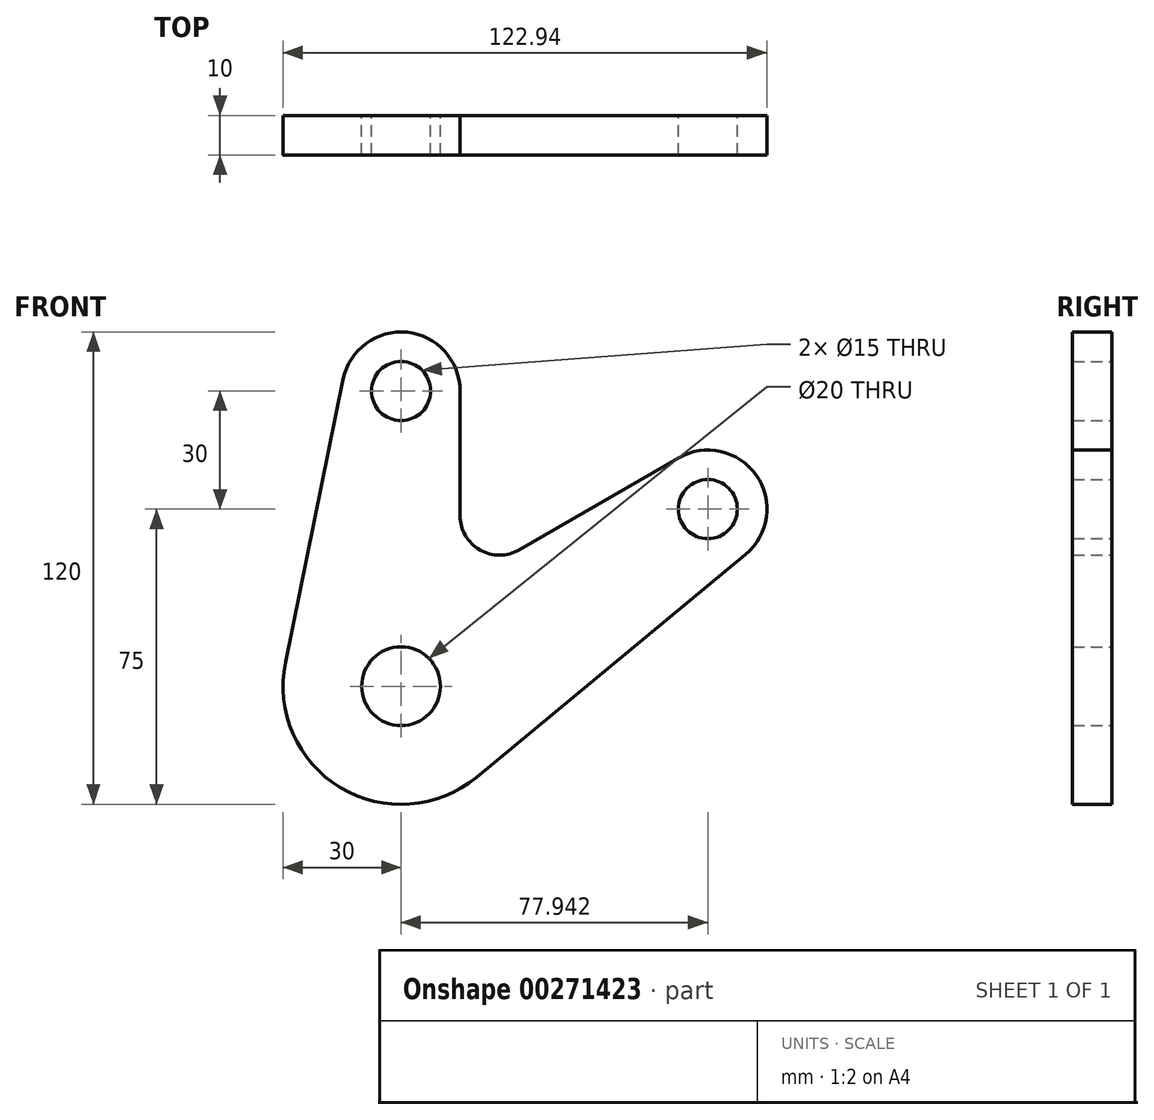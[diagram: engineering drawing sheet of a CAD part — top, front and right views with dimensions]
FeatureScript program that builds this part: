
annotation { "Feature Type Name" : "Feature", "Feature Type Description" : "" }
export const myFeature = defineFeature(function(context is Context, id is Id, definition is map)
    precondition{}
    {
        {
            var Q0;
            Q0=qCreatedBy(makeId("Front.planeOp"),FACE);
            var sketch = newSketch(context, id + "F0", { "sketchPlane" : qUnion([Q0])});
            skCircle(sketch, "E0", {"center": v(0, 0) * mm, "radius": 10 * mm});
            skCircle(sketch, "E1", {"center": v(0, 75) * mm, "radius": 7.5 * mm});
            skCircle(sketch, "E2", {"center": v(77.94, 45) * mm, "radius": 7.5 * mm});
            skLineSegment(sketch, "E3", {"start": v(70.44, 58) * mm, "end": v(30, 34.64) * mm});
            skLineSegment(sketch, "E4", {"start": v(87.5, 33.44) * mm, "end": v(19.12, -23.12) * mm});
            skLineSegment(sketch, "E5", {"start": v(-14.7, 78) * mm, "end": v(-29.4, 6) * mm});
            skArc(sketch, "E6", {"start": v(-29.4, 6) * mm, "mid": v(-15.44, -25.72) * mm, "end": v(19.12, -23.12) * mm});
            skLineSegment(sketch, "E7", {"start": v(15, 75) * mm, "end": v(15, 43.3) * mm});
            skArc(sketch, "E8.filletArc", {"start": v(15, 43.3) * mm, "mid": v(20, 34.64) * mm, "end": v(30, 34.64) * mm});
            skArc(sketch, "E9", {"start": v(-14.7, 78) * mm, "mid": v(1.5, 89.92) * mm, "end": v(15, 75) * mm});
            skArc(sketch, "E10", {"start": v(70.44, 58) * mm, "mid": v(90.26, 53.56) * mm, "end": v(87.5, 33.44) * mm});
            skLineSegment(sketch, "E11", {"start": v(77.94, 45) * mm, "end": v(0, 0) * mm, "construction": true});
            skLineSegment(sketch, "E12", {"start": v(0, 75) * mm, "end": v(0, 0) * mm, "construction": true});
            skSolve(sketch);
        }
        {
            var Q0;
            Q0=makeQuery(id+"F0.imprint","IMPRINT",FACE,{"disambiguationData":[TD([[makeQuery(id+"F0.imprint","IMPRINT",EDGE,{"derivedFrom":sQuery(id+"F0.wireOp",EDGE,"E0")}),-1.0]])]});
            extrude(context, id + "F1", {"entities" : qUnion([Q0]), "depth" : 10 * mm});
        }
    });
